# Revit family: Legrand_Lighting_Management_SCS_Presence_Sensor_Ceiling
name_source: partatom
category: Dispositifs d'éclairage
units: mm (PartAtom-declared; Revit-internal decimal feet)

## family parameters
Conserver l'orientation des annotations = Non
Cote de connecteur circulaire = Utiliser le diamètre
Couper avec des vides une fois chargée = Non
Hôte = Face
Partagée = Non
Point de calcul de pièce = Non
Type d'élément = Normal

## types (2) — shared parameters
Alarm function = Non
Collecteur de terre = Non
Colour = White
Constant light control = Oui
Cosses d'artère secondaire = Non
Detection angle horizontal (MAX) (°) = 360
Dim function with dimmer basic element = Non
Elévation par défaut = 1219 mm
Fabricant = Legrand
Forced switch off = Non
General Conditions of Use = https://export.legrand.com
HVAC-control = Non
Liaison neutre = Non
Max. duty cycle (mn) = 256
Max. transmission range sideways (m) = 4
Maximum mounting height (m) = 2.5
Min. switch-on time (s) = 30
Model = Movement sensor
Mounting method = Flush mounted (plaster)
RAL-number (akin) = 9003
Remote operation = Non
Response value luminosity adjustable = Oui
Response value sensitivity adjustable = Oui
Substation input = Non
Suitable for wireless transmission = Non
URL = http://www.legrandoc.com
zero-valued in all types: Detection angle horizontal (MIN) (°), Frequency (MAX) (Hz), Frequency (MIN) (Hz), Max. starting current (A), Max. switching power (W), Max. transmission range frontally (m), Nominal voltage (V), Response value luminosity (MAX) (lx), Response value luminosity (MIN) (lx), Temperature (MAX) (°C), Temperature (MIN) (°C)

## per-type parameters (varying)
| type | Description | Diameter detection range on floor (m) | Modèle | Mouvement SCS PIR 360° 4m | Présence SCS PIR/US 360° 4m |
| SCS PIR motion 360° 4m | Lighting management--wall mounting-IR-360°-for 47 m² areas - flush mounting | 8 | 048820 | Oui | Non |
| SCS PIR/US presence 360° 4m | Lighting management--wall mounting-DT-360°-for 93 m² areas - flush mounting | 11 | 048822 | Non | Oui |
